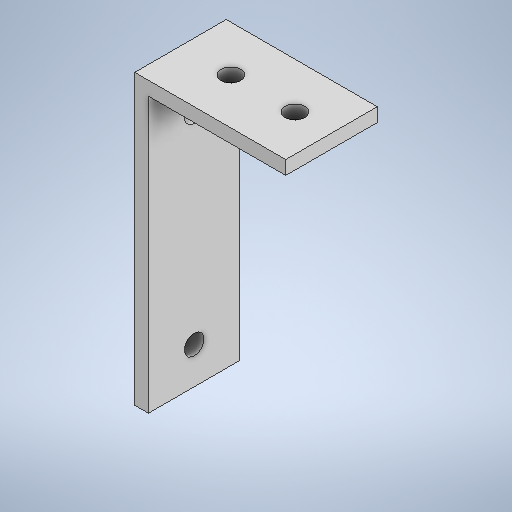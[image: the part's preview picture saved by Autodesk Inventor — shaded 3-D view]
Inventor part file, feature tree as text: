
AUTODESK INVENTOR PART (.ipt)
format: ipt  version: 2025.2 (Build 292293000, 293)  size: 254,976 bytes
history: native  units: mm
features: extrude x3, sketch x3, plane x1
ambient origin geometry x8: Origin, YZ Plane, XZ Plane, XY Plane, X Axis, Y Axis, Z Axis, Center Point
bodies: Solid1 (feature_tree)
feature tree (7):
  extrude  "Extrusion1"  Depth=60.0mm
  extrude  "Extrusion2"  Depth=3.0mm
  extrude  "Extrusion3"  Depth=20.0mm
  plane  "Work Plane1"
  sketch  "Sketch1"  dims[d0=30.0mm d1=60.0mm]
  sketch  "Sketch2"  dims[d2=3.0mm d3=3.0mm]
  sketch  "Sketch3"  dims[d4=20.0mm d5=0.0mm d6=8.0mm d7=8.0mm d8=4.3mm d9=4.3mm d10=0.0mm d11=0.0mm d12=8.0mm d13=8.0mm d14=4.3mm d15=4.3mm d16=0.0mm d17=0.0mm d18=-10.0mm]
